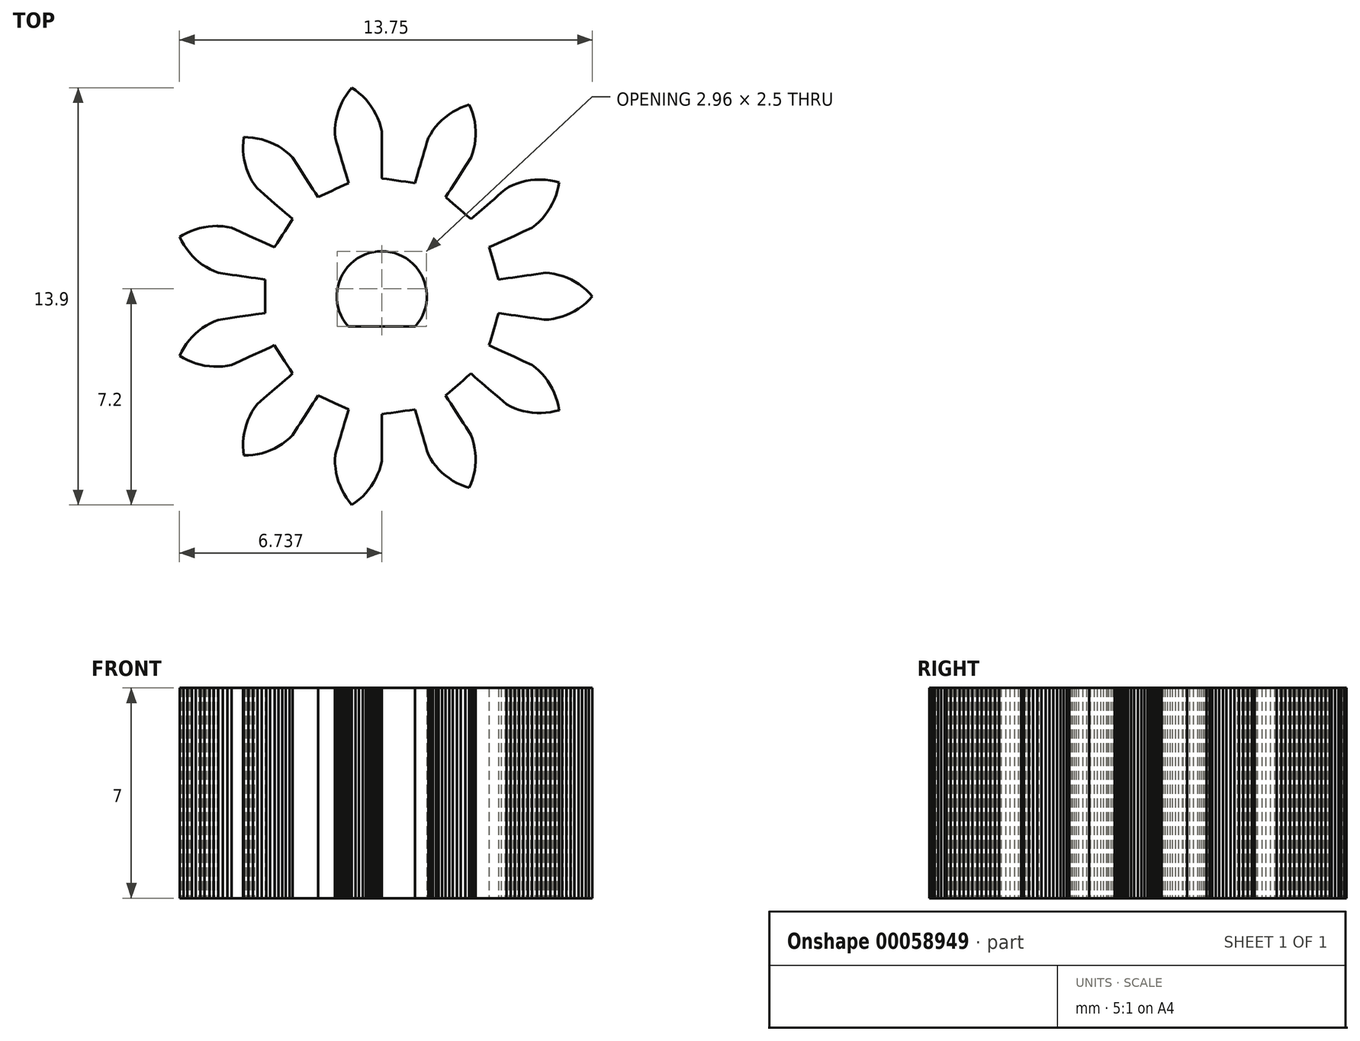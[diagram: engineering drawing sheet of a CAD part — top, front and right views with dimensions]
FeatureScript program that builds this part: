
annotation { "Feature Type Name" : "Feature", "Feature Type Description" : "" }
export const myFeature = defineFeature(function(context is Context, id is Id, definition is map)
    precondition{}
    {
        {
            var Q0;
            Q0=qCreatedBy(makeId("Top.planeOp"),FACE);
            var sketch = newSketch(context, id + "F0", { "sketchPlane" : qUnion([Q0])});
            skLineSegment(sketch, "E0", {"start": v(2.79, -0.56) * mm, "end": v(2.89, -0.57) * mm});
            skLineSegment(sketch, "E1", {"start": v(2.89, -0.57) * mm, "end": v(3.05, -0.6) * mm});
            skLineSegment(sketch, "E2", {"start": v(3.05, -0.6) * mm, "end": v(3.2, -0.62) * mm});
            skLineSegment(sketch, "E3", {"start": v(3.2, -0.62) * mm, "end": v(3.36, -0.64) * mm});
            skLineSegment(sketch, "E4", {"start": v(3.36, -0.64) * mm, "end": v(3.51, -0.66) * mm});
            skLineSegment(sketch, "E5", {"start": v(3.51, -0.66) * mm, "end": v(3.67, -0.69) * mm});
            skLineSegment(sketch, "E6", {"start": v(3.67, -0.69) * mm, "end": v(3.82, -0.7) * mm});
            skLineSegment(sketch, "E7", {"start": v(3.82, -0.7) * mm, "end": v(3.98, -0.73) * mm});
            skLineSegment(sketch, "E8", {"start": v(3.98, -0.73) * mm, "end": v(4.13, -0.75) * mm});
            skLineSegment(sketch, "E9", {"start": v(4.13, -0.75) * mm, "end": v(4.29, -0.78) * mm});
            skLineSegment(sketch, "E10", {"start": v(4.29, -0.78) * mm, "end": v(4.46, -0.77) * mm});
            skLineSegment(sketch, "E11", {"start": v(4.46, -0.77) * mm, "end": v(4.62, -0.75) * mm});
            skLineSegment(sketch, "E12", {"start": v(4.62, -0.75) * mm, "end": v(4.76, -0.72) * mm});
            skLineSegment(sketch, "E13", {"start": v(4.76, -0.72) * mm, "end": v(4.9, -0.67) * mm});
            skLineSegment(sketch, "E14", {"start": v(4.9, -0.67) * mm, "end": v(5.04, -0.63) * mm});
            skLineSegment(sketch, "E15", {"start": v(5.04, -0.63) * mm, "end": v(5.19, -0.56) * mm});
            skLineSegment(sketch, "E16", {"start": v(5.19, -0.56) * mm, "end": v(5.31, -0.5) * mm});
            skLineSegment(sketch, "E17", {"start": v(5.31, -0.5) * mm, "end": v(5.45, -0.41) * mm});
            skLineSegment(sketch, "E18", {"start": v(5.45, -0.41) * mm, "end": v(5.56, -0.33) * mm});
            skLineSegment(sketch, "E19", {"start": v(5.56, -0.33) * mm, "end": v(5.69, -0.23) * mm});
            skLineSegment(sketch, "E20", {"start": v(5.69, -0.23) * mm, "end": v(5.8, -0.13) * mm});
            skLineSegment(sketch, "E21", {"start": v(5.8, -0.13) * mm, "end": v(5.9, -0.02) * mm});
            skLineSegment(sketch, "E22", {"start": v(5.9, -0.02) * mm, "end": v(5.91, 0) * mm});
            skLineSegment(sketch, "E23", {"start": v(5.91, 0) * mm, "end": v(5.8, 0.12) * mm});
            skLineSegment(sketch, "E24", {"start": v(5.8, 0.12) * mm, "end": v(5.7, 0.22) * mm});
            skLineSegment(sketch, "E25", {"start": v(5.7, 0.22) * mm, "end": v(5.58, 0.32) * mm});
            skLineSegment(sketch, "E26", {"start": v(5.58, 0.32) * mm, "end": v(5.47, 0.4) * mm});
            skLineSegment(sketch, "E27", {"start": v(5.47, 0.4) * mm, "end": v(5.33, 0.48) * mm});
            skLineSegment(sketch, "E28", {"start": v(5.33, 0.48) * mm, "end": v(5.2, 0.55) * mm});
            skLineSegment(sketch, "E29", {"start": v(5.2, 0.55) * mm, "end": v(5.06, 0.62) * mm});
            skLineSegment(sketch, "E30", {"start": v(5.06, 0.62) * mm, "end": v(4.93, 0.67) * mm});
            skLineSegment(sketch, "E31", {"start": v(4.93, 0.67) * mm, "end": v(4.78, 0.71) * mm});
            skLineSegment(sketch, "E32", {"start": v(4.78, 0.71) * mm, "end": v(4.64, 0.75) * mm});
            skLineSegment(sketch, "E33", {"start": v(4.64, 0.75) * mm, "end": v(4.48, 0.77) * mm});
            skLineSegment(sketch, "E34", {"start": v(4.48, 0.77) * mm, "end": v(4.34, 0.78) * mm});
            skLineSegment(sketch, "E35", {"start": v(4.34, 0.78) * mm, "end": v(4.19, 0.76) * mm});
            skLineSegment(sketch, "E36", {"start": v(4.19, 0.76) * mm, "end": v(4.03, 0.74) * mm});
            skLineSegment(sketch, "E37", {"start": v(4.03, 0.74) * mm, "end": v(3.87, 0.72) * mm});
            skLineSegment(sketch, "E38", {"start": v(3.87, 0.72) * mm, "end": v(3.72, 0.7) * mm});
            skLineSegment(sketch, "E39", {"start": v(3.72, 0.7) * mm, "end": v(3.56, 0.67) * mm});
            skLineSegment(sketch, "E40", {"start": v(3.56, 0.67) * mm, "end": v(3.4, 0.65) * mm});
            skLineSegment(sketch, "E41", {"start": v(3.4, 0.65) * mm, "end": v(3.25, 0.63) * mm});
            skLineSegment(sketch, "E42", {"start": v(3.25, 0.63) * mm, "end": v(3.1, 0.6) * mm});
            skLineSegment(sketch, "E43", {"start": v(3.1, 0.6) * mm, "end": v(2.94, 0.58) * mm});
            skLineSegment(sketch, "E44", {"start": v(2.94, 0.58) * mm, "end": v(2.79, 0.56) * mm});
            skLineSegment(sketch, "E45", {"start": v(2.79, 0.56) * mm, "end": v(2.74, 0.71) * mm});
            skLineSegment(sketch, "E46", {"start": v(2.74, 0.71) * mm, "end": v(2.7, 0.86) * mm});
            skLineSegment(sketch, "E47", {"start": v(2.7, 0.86) * mm, "end": v(2.65, 1.01) * mm});
            skLineSegment(sketch, "E48", {"start": v(2.65, 1.01) * mm, "end": v(2.6, 1.16) * mm});
            skLineSegment(sketch, "E49", {"start": v(2.6, 1.16) * mm, "end": v(2.56, 1.31) * mm});
            skLineSegment(sketch, "E50", {"start": v(2.56, 1.31) * mm, "end": v(2.52, 1.47) * mm});
            skLineSegment(sketch, "E51", {"start": v(2.52, 1.47) * mm, "end": v(2.48, 1.62) * mm});
            skLineSegment(sketch, "E52", {"start": v(2.48, 1.62) * mm, "end": v(2.47, 1.63) * mm});
            skLineSegment(sketch, "E53", {"start": v(2.47, 1.63) * mm, "end": v(2.61, 1.7) * mm});
            skLineSegment(sketch, "E54", {"start": v(2.61, 1.7) * mm, "end": v(2.76, 1.76) * mm});
            skLineSegment(sketch, "E55", {"start": v(2.76, 1.76) * mm, "end": v(2.9, 1.83) * mm});
            skLineSegment(sketch, "E56", {"start": v(2.9, 1.83) * mm, "end": v(3.04, 1.9) * mm});
            skLineSegment(sketch, "E57", {"start": v(3.04, 1.9) * mm, "end": v(3.19, 1.96) * mm});
            skLineSegment(sketch, "E58", {"start": v(3.19, 1.96) * mm, "end": v(3.33, 2.02) * mm});
            skLineSegment(sketch, "E59", {"start": v(3.33, 2.02) * mm, "end": v(3.47, 2.09) * mm});
            skLineSegment(sketch, "E60", {"start": v(3.47, 2.09) * mm, "end": v(3.61, 2.15) * mm});
            skLineSegment(sketch, "E61", {"start": v(3.61, 2.15) * mm, "end": v(3.76, 2.22) * mm});
            skLineSegment(sketch, "E62", {"start": v(3.76, 2.22) * mm, "end": v(3.9, 2.28) * mm});
            skLineSegment(sketch, "E63", {"start": v(3.9, 2.28) * mm, "end": v(4.02, 2.38) * mm});
            skLineSegment(sketch, "E64", {"start": v(4.02, 2.38) * mm, "end": v(4.13, 2.48) * mm});
            skLineSegment(sketch, "E65", {"start": v(4.13, 2.48) * mm, "end": v(4.24, 2.6) * mm});
            skLineSegment(sketch, "E66", {"start": v(4.24, 2.6) * mm, "end": v(4.33, 2.7) * mm});
            skLineSegment(sketch, "E67", {"start": v(4.33, 2.7) * mm, "end": v(4.43, 2.83) * mm});
            skLineSegment(sketch, "E68", {"start": v(4.43, 2.83) * mm, "end": v(4.5, 2.95) * mm});
            skLineSegment(sketch, "E69", {"start": v(4.5, 2.95) * mm, "end": v(4.58, 3.09) * mm});
            skLineSegment(sketch, "E70", {"start": v(4.58, 3.09) * mm, "end": v(4.64, 3.22) * mm});
            skLineSegment(sketch, "E71", {"start": v(4.64, 3.22) * mm, "end": v(4.7, 3.36) * mm});
            skLineSegment(sketch, "E72", {"start": v(4.7, 3.36) * mm, "end": v(4.74, 3.5) * mm});
            skLineSegment(sketch, "E73", {"start": v(4.74, 3.5) * mm, "end": v(4.78, 3.65) * mm});
            skLineSegment(sketch, "E74", {"start": v(4.78, 3.65) * mm, "end": v(4.8, 3.8) * mm});
            skLineSegment(sketch, "E75", {"start": v(4.8, 3.8) * mm, "end": v(4.65, 3.83) * mm});
            skLineSegment(sketch, "E76", {"start": v(4.65, 3.83) * mm, "end": v(4.5, 3.86) * mm});
            skLineSegment(sketch, "E77", {"start": v(4.5, 3.86) * mm, "end": v(4.35, 3.88) * mm});
            skLineSegment(sketch, "E78", {"start": v(4.35, 3.88) * mm, "end": v(4.2, 3.89) * mm});
            skLineSegment(sketch, "E79", {"start": v(4.2, 3.89) * mm, "end": v(4.15, 3.89) * mm});
            skLineSegment(sketch, "E80", {"start": v(4.15, 3.89) * mm, "end": v(4, 3.88) * mm});
            skLineSegment(sketch, "E81", {"start": v(4, 3.88) * mm, "end": v(3.85, 3.87) * mm});
            skLineSegment(sketch, "E82", {"start": v(3.85, 3.87) * mm, "end": v(3.7, 3.84) * mm});
            skLineSegment(sketch, "E83", {"start": v(3.7, 3.84) * mm, "end": v(3.55, 3.8) * mm});
            skLineSegment(sketch, "E84", {"start": v(3.55, 3.8) * mm, "end": v(3.4, 3.76) * mm});
            skLineSegment(sketch, "E85", {"start": v(3.4, 3.76) * mm, "end": v(3.27, 3.7) * mm});
            skLineSegment(sketch, "E86", {"start": v(3.27, 3.7) * mm, "end": v(3.13, 3.64) * mm});
            skLineSegment(sketch, "E87", {"start": v(3.13, 3.64) * mm, "end": v(3, 3.55) * mm});
            skLineSegment(sketch, "E88", {"start": v(3, 3.55) * mm, "end": v(2.88, 3.45) * mm});
            skLineSegment(sketch, "E89", {"start": v(2.88, 3.45) * mm, "end": v(2.76, 3.35) * mm});
            skLineSegment(sketch, "E90", {"start": v(2.76, 3.35) * mm, "end": v(2.64, 3.24) * mm});
            skLineSegment(sketch, "E91", {"start": v(2.64, 3.24) * mm, "end": v(2.52, 3.14) * mm});
            skLineSegment(sketch, "E92", {"start": v(2.52, 3.14) * mm, "end": v(2.4, 3.04) * mm});
            skLineSegment(sketch, "E93", {"start": v(2.4, 3.04) * mm, "end": v(2.28, 2.93) * mm});
            skLineSegment(sketch, "E94", {"start": v(2.28, 2.93) * mm, "end": v(2.16, 2.83) * mm});
            skLineSegment(sketch, "E95", {"start": v(2.16, 2.83) * mm, "end": v(2.04, 2.73) * mm});
            skLineSegment(sketch, "E96", {"start": v(2.04, 2.73) * mm, "end": v(1.93, 2.62) * mm});
            skLineSegment(sketch, "E97", {"start": v(1.93, 2.62) * mm, "end": v(1.87, 2.57) * mm});
            skLineSegment(sketch, "E98", {"start": v(1.87, 2.57) * mm, "end": v(1.75, 2.68) * mm});
            skLineSegment(sketch, "E99", {"start": v(1.75, 2.68) * mm, "end": v(1.63, 2.78) * mm});
            skLineSegment(sketch, "E100", {"start": v(1.63, 2.78) * mm, "end": v(1.5, 2.88) * mm});
            skLineSegment(sketch, "E101", {"start": v(1.5, 2.88) * mm, "end": v(1.4, 2.99) * mm});
            skLineSegment(sketch, "E102", {"start": v(1.4, 2.99) * mm, "end": v(1.27, 3.09) * mm});
            skLineSegment(sketch, "E103", {"start": v(1.27, 3.09) * mm, "end": v(1.15, 3.2) * mm});
            skLineSegment(sketch, "E104", {"start": v(1.15, 3.2) * mm, "end": v(1.03, 3.3) * mm});
            skLineSegment(sketch, "E105", {"start": v(1.03, 3.3) * mm, "end": v(1.02, 3.3) * mm});
            skLineSegment(sketch, "E106", {"start": v(1.02, 3.3) * mm, "end": v(1.1, 3.44) * mm});
            skLineSegment(sketch, "E107", {"start": v(1.1, 3.44) * mm, "end": v(1.2, 3.57) * mm});
            skLineSegment(sketch, "E108", {"start": v(1.2, 3.57) * mm, "end": v(1.28, 3.7) * mm});
            skLineSegment(sketch, "E109", {"start": v(1.28, 3.7) * mm, "end": v(1.36, 3.83) * mm});
            skLineSegment(sketch, "E110", {"start": v(1.36, 3.83) * mm, "end": v(1.45, 3.97) * mm});
            skLineSegment(sketch, "E111", {"start": v(1.45, 3.97) * mm, "end": v(1.53, 4.1) * mm});
            skLineSegment(sketch, "E112", {"start": v(1.53, 4.1) * mm, "end": v(1.62, 4.23) * mm});
            skLineSegment(sketch, "E113", {"start": v(1.62, 4.23) * mm, "end": v(1.7, 4.36) * mm});
            skLineSegment(sketch, "E114", {"start": v(1.7, 4.36) * mm, "end": v(1.79, 4.5) * mm});
            skLineSegment(sketch, "E115", {"start": v(1.79, 4.5) * mm, "end": v(1.87, 4.63) * mm});
            skLineSegment(sketch, "E116", {"start": v(1.87, 4.63) * mm, "end": v(1.92, 4.78) * mm});
            skLineSegment(sketch, "E117", {"start": v(1.92, 4.78) * mm, "end": v(1.96, 4.91) * mm});
            skLineSegment(sketch, "E118", {"start": v(1.96, 4.91) * mm, "end": v(2, 5.07) * mm});
            skLineSegment(sketch, "E119", {"start": v(2, 5.07) * mm, "end": v(2.01, 5.21) * mm});
            skLineSegment(sketch, "E120", {"start": v(2.01, 5.21) * mm, "end": v(2.02, 5.37) * mm});
            skLineSegment(sketch, "E121", {"start": v(2.02, 5.37) * mm, "end": v(2.02, 5.51) * mm});
            skLineSegment(sketch, "E122", {"start": v(2.02, 5.51) * mm, "end": v(2, 5.67) * mm});
            skLineSegment(sketch, "E123", {"start": v(2, 5.67) * mm, "end": v(2, 5.81) * mm});
            skLineSegment(sketch, "E124", {"start": v(2, 5.81) * mm, "end": v(1.96, 5.96) * mm});
            skLineSegment(sketch, "E125", {"start": v(1.96, 5.96) * mm, "end": v(1.92, 6.1) * mm});
            skLineSegment(sketch, "E126", {"start": v(1.92, 6.1) * mm, "end": v(1.87, 6.25) * mm});
            skLineSegment(sketch, "E127", {"start": v(1.87, 6.25) * mm, "end": v(1.81, 6.38) * mm});
            skLineSegment(sketch, "E128", {"start": v(1.81, 6.38) * mm, "end": v(1.66, 6.33) * mm});
            skLineSegment(sketch, "E129", {"start": v(1.66, 6.33) * mm, "end": v(1.53, 6.28) * mm});
            skLineSegment(sketch, "E130", {"start": v(1.53, 6.28) * mm, "end": v(1.39, 6.21) * mm});
            skLineSegment(sketch, "E131", {"start": v(1.39, 6.21) * mm, "end": v(1.26, 6.14) * mm});
            skLineSegment(sketch, "E132", {"start": v(1.26, 6.14) * mm, "end": v(1.13, 6.06) * mm});
            skLineSegment(sketch, "E133", {"start": v(1.13, 6.06) * mm, "end": v(1.02, 5.97) * mm});
            skLineSegment(sketch, "E134", {"start": v(1.02, 5.97) * mm, "end": v(0.9, 5.87) * mm});
            skLineSegment(sketch, "E135", {"start": v(0.9, 5.87) * mm, "end": v(0.8, 5.77) * mm});
            skLineSegment(sketch, "E136", {"start": v(0.8, 5.77) * mm, "end": v(0.7, 5.65) * mm});
            skLineSegment(sketch, "E137", {"start": v(0.7, 5.65) * mm, "end": v(0.6, 5.53) * mm});
            skLineSegment(sketch, "E138", {"start": v(0.6, 5.53) * mm, "end": v(0.52, 5.4) * mm});
            skLineSegment(sketch, "E139", {"start": v(0.52, 5.4) * mm, "end": v(0.45, 5.28) * mm});
            skLineSegment(sketch, "E140", {"start": v(0.45, 5.28) * mm, "end": v(0.4, 5.13) * mm});
            skLineSegment(sketch, "E141", {"start": v(0.4, 5.13) * mm, "end": v(0.36, 4.98) * mm});
            skLineSegment(sketch, "E142", {"start": v(0.36, 4.98) * mm, "end": v(0.31, 4.83) * mm});
            skLineSegment(sketch, "E143", {"start": v(0.31, 4.83) * mm, "end": v(0.27, 4.67) * mm});
            skLineSegment(sketch, "E144", {"start": v(0.27, 4.67) * mm, "end": v(0.22, 4.52) * mm});
            skLineSegment(sketch, "E145", {"start": v(0.22, 4.52) * mm, "end": v(0.18, 4.37) * mm});
            skLineSegment(sketch, "E146", {"start": v(0.18, 4.37) * mm, "end": v(0.14, 4.22) * mm});
            skLineSegment(sketch, "E147", {"start": v(0.14, 4.22) * mm, "end": v(0.1, 4.07) * mm});
            skLineSegment(sketch, "E148", {"start": v(0.1, 4.07) * mm, "end": v(0.05, 3.92) * mm});
            skLineSegment(sketch, "E149", {"start": v(0.05, 3.92) * mm, "end": v(0, 3.77) * mm});
            skLineSegment(sketch, "E150", {"start": v(0, 3.77) * mm, "end": v(-0.15, 3.8) * mm});
            skLineSegment(sketch, "E151", {"start": v(-0.15, 3.8) * mm, "end": v(-0.3, 3.81) * mm});
            skLineSegment(sketch, "E152", {"start": v(-0.3, 3.81) * mm, "end": v(-0.46, 3.84) * mm});
            skLineSegment(sketch, "E153", {"start": v(-0.46, 3.84) * mm, "end": v(-0.62, 3.86) * mm});
            skLineSegment(sketch, "E154", {"start": v(-0.62, 3.86) * mm, "end": v(-0.78, 3.88) * mm});
            skLineSegment(sketch, "E155", {"start": v(-0.78, 3.88) * mm, "end": v(-0.93, 3.9) * mm});
            skLineSegment(sketch, "E156", {"start": v(-0.93, 3.9) * mm, "end": v(-1.09, 3.93) * mm});
            skLineSegment(sketch, "E157", {"start": v(-1.09, 3.93) * mm, "end": v(-1.1, 3.93) * mm});
            skLineSegment(sketch, "E158", {"start": v(-1.1, 3.93) * mm, "end": v(-1.1, 4.09) * mm});
            skLineSegment(sketch, "E159", {"start": v(-1.1, 4.09) * mm, "end": v(-1.1, 4.24) * mm});
            skLineSegment(sketch, "E160", {"start": v(-1.1, 4.24) * mm, "end": v(-1.1, 4.4) * mm});
            skLineSegment(sketch, "E161", {"start": v(-1.1, 4.4) * mm, "end": v(-1.1, 4.56) * mm});
            skLineSegment(sketch, "E162", {"start": v(-1.1, 4.56) * mm, "end": v(-1.1, 4.71) * mm});
            skLineSegment(sketch, "E163", {"start": v(-1.1, 4.71) * mm, "end": v(-1.1, 4.87) * mm});
            skLineSegment(sketch, "E164", {"start": v(-1.1, 4.87) * mm, "end": v(-1.1, 5.03) * mm});
            skLineSegment(sketch, "E165", {"start": v(-1.1, 5.03) * mm, "end": v(-1.1, 5.19) * mm});
            skLineSegment(sketch, "E166", {"start": v(-1.1, 5.19) * mm, "end": v(-1.1, 5.34) * mm});
            skLineSegment(sketch, "E167", {"start": v(-1.1, 5.34) * mm, "end": v(-1.1, 5.5) * mm});
            skLineSegment(sketch, "E168", {"start": v(-1.1, 5.5) * mm, "end": v(-1.14, 5.65) * mm});
            skLineSegment(sketch, "E169", {"start": v(-1.14, 5.65) * mm, "end": v(-1.18, 5.8) * mm});
            skLineSegment(sketch, "E170", {"start": v(-1.18, 5.8) * mm, "end": v(-1.24, 5.94) * mm});
            skLineSegment(sketch, "E171", {"start": v(-1.24, 5.94) * mm, "end": v(-1.3, 6.07) * mm});
            skLineSegment(sketch, "E172", {"start": v(-1.3, 6.07) * mm, "end": v(-1.38, 6.2) * mm});
            skLineSegment(sketch, "E173", {"start": v(-1.38, 6.2) * mm, "end": v(-1.45, 6.33) * mm});
            skLineSegment(sketch, "E174", {"start": v(-1.45, 6.33) * mm, "end": v(-1.55, 6.45) * mm});
            skLineSegment(sketch, "E175", {"start": v(-1.55, 6.45) * mm, "end": v(-1.64, 6.56) * mm});
            skLineSegment(sketch, "E176", {"start": v(-1.64, 6.56) * mm, "end": v(-1.75, 6.67) * mm});
            skLineSegment(sketch, "E177", {"start": v(-1.75, 6.67) * mm, "end": v(-1.86, 6.77) * mm});
            skLineSegment(sketch, "E178", {"start": v(-1.86, 6.77) * mm, "end": v(-1.98, 6.86) * mm});
            skLineSegment(sketch, "E179", {"start": v(-1.98, 6.86) * mm, "end": v(-2.1, 6.95) * mm});
            skLineSegment(sketch, "E180", {"start": v(-2.1, 6.95) * mm, "end": v(-2.2, 6.82) * mm});
            skLineSegment(sketch, "E181", {"start": v(-2.2, 6.82) * mm, "end": v(-2.29, 6.7) * mm});
            skLineSegment(sketch, "E182", {"start": v(-2.29, 6.7) * mm, "end": v(-2.37, 6.57) * mm});
            skLineSegment(sketch, "E183", {"start": v(-2.37, 6.57) * mm, "end": v(-2.43, 6.45) * mm});
            skLineSegment(sketch, "E184", {"start": v(-2.43, 6.45) * mm, "end": v(-2.5, 6.3) * mm});
            skLineSegment(sketch, "E185", {"start": v(-2.5, 6.3) * mm, "end": v(-2.55, 6.17) * mm});
            skLineSegment(sketch, "E186", {"start": v(-2.55, 6.17) * mm, "end": v(-2.6, 6.02) * mm});
            skLineSegment(sketch, "E187", {"start": v(-2.6, 6.02) * mm, "end": v(-2.62, 5.88) * mm});
            skLineSegment(sketch, "E188", {"start": v(-2.62, 5.88) * mm, "end": v(-2.65, 5.72) * mm});
            skLineSegment(sketch, "E189", {"start": v(-2.65, 5.72) * mm, "end": v(-2.66, 5.58) * mm});
            skLineSegment(sketch, "E190", {"start": v(-2.66, 5.58) * mm, "end": v(-2.66, 5.42) * mm});
            skLineSegment(sketch, "E191", {"start": v(-2.66, 5.42) * mm, "end": v(-2.65, 5.28) * mm});
            skLineSegment(sketch, "E192", {"start": v(-2.65, 5.28) * mm, "end": v(-2.6, 5.13) * mm});
            skLineSegment(sketch, "E193", {"start": v(-2.6, 5.13) * mm, "end": v(-2.56, 4.98) * mm});
            skLineSegment(sketch, "E194", {"start": v(-2.56, 4.98) * mm, "end": v(-2.52, 4.83) * mm});
            skLineSegment(sketch, "E195", {"start": v(-2.52, 4.83) * mm, "end": v(-2.48, 4.67) * mm});
            skLineSegment(sketch, "E196", {"start": v(-2.48, 4.67) * mm, "end": v(-2.43, 4.52) * mm});
            skLineSegment(sketch, "E197", {"start": v(-2.43, 4.52) * mm, "end": v(-2.39, 4.37) * mm});
            skLineSegment(sketch, "E198", {"start": v(-2.39, 4.37) * mm, "end": v(-2.34, 4.22) * mm});
            skLineSegment(sketch, "E199", {"start": v(-2.34, 4.22) * mm, "end": v(-2.3, 4.07) * mm});
            skLineSegment(sketch, "E200", {"start": v(-2.3, 4.07) * mm, "end": v(-2.25, 3.92) * mm});
            skLineSegment(sketch, "E201", {"start": v(-2.25, 3.92) * mm, "end": v(-2.21, 3.77) * mm});
            skLineSegment(sketch, "E202", {"start": v(-2.21, 3.77) * mm, "end": v(-2.35, 3.7) * mm});
            skLineSegment(sketch, "E203", {"start": v(-2.35, 3.7) * mm, "end": v(-2.5, 3.64) * mm});
            skLineSegment(sketch, "E204", {"start": v(-2.5, 3.64) * mm, "end": v(-2.64, 3.57) * mm});
            skLineSegment(sketch, "E205", {"start": v(-2.64, 3.57) * mm, "end": v(-2.78, 3.5) * mm});
            skLineSegment(sketch, "E206", {"start": v(-2.78, 3.5) * mm, "end": v(-2.93, 3.44) * mm});
            skLineSegment(sketch, "E207", {"start": v(-2.93, 3.44) * mm, "end": v(-3.07, 3.38) * mm});
            skLineSegment(sketch, "E208", {"start": v(-3.07, 3.38) * mm, "end": v(-3.21, 3.31) * mm});
            skLineSegment(sketch, "E209", {"start": v(-3.21, 3.31) * mm, "end": v(-3.23, 3.3) * mm});
            skLineSegment(sketch, "E210", {"start": v(-3.23, 3.3) * mm, "end": v(-3.31, 3.44) * mm});
            skLineSegment(sketch, "E211", {"start": v(-3.31, 3.44) * mm, "end": v(-3.4, 3.57) * mm});
            skLineSegment(sketch, "E212", {"start": v(-3.4, 3.57) * mm, "end": v(-3.48, 3.7) * mm});
            skLineSegment(sketch, "E213", {"start": v(-3.48, 3.7) * mm, "end": v(-3.57, 3.83) * mm});
            skLineSegment(sketch, "E214", {"start": v(-3.57, 3.83) * mm, "end": v(-3.65, 3.97) * mm});
            skLineSegment(sketch, "E215", {"start": v(-3.65, 3.97) * mm, "end": v(-3.74, 4.1) * mm});
            skLineSegment(sketch, "E216", {"start": v(-3.74, 4.1) * mm, "end": v(-3.82, 4.23) * mm});
            skLineSegment(sketch, "E217", {"start": v(-3.82, 4.23) * mm, "end": v(-3.9, 4.36) * mm});
            skLineSegment(sketch, "E218", {"start": v(-3.9, 4.36) * mm, "end": v(-4, 4.5) * mm});
            skLineSegment(sketch, "E219", {"start": v(-4, 4.5) * mm, "end": v(-4.08, 4.63) * mm});
            skLineSegment(sketch, "E220", {"start": v(-4.08, 4.63) * mm, "end": v(-4.2, 4.74) * mm});
            skLineSegment(sketch, "E221", {"start": v(-4.2, 4.74) * mm, "end": v(-4.3, 4.83) * mm});
            skLineSegment(sketch, "E222", {"start": v(-4.3, 4.83) * mm, "end": v(-4.43, 4.92) * mm});
            skLineSegment(sketch, "E223", {"start": v(-4.43, 4.92) * mm, "end": v(-4.55, 5) * mm});
            skLineSegment(sketch, "E224", {"start": v(-4.55, 5) * mm, "end": v(-4.69, 5.07) * mm});
            skLineSegment(sketch, "E225", {"start": v(-4.69, 5.07) * mm, "end": v(-4.82, 5.13) * mm});
            skLineSegment(sketch, "E226", {"start": v(-4.82, 5.13) * mm, "end": v(-4.97, 5.19) * mm});
            skLineSegment(sketch, "E227", {"start": v(-4.97, 5.19) * mm, "end": v(-5.1, 5.23) * mm});
            skLineSegment(sketch, "E228", {"start": v(-5.1, 5.23) * mm, "end": v(-5.26, 5.26) * mm});
            skLineSegment(sketch, "E229", {"start": v(-5.26, 5.26) * mm, "end": v(-5.4, 5.29) * mm});
            skLineSegment(sketch, "E230", {"start": v(-5.4, 5.29) * mm, "end": v(-5.56, 5.3) * mm});
            skLineSegment(sketch, "E231", {"start": v(-5.56, 5.3) * mm, "end": v(-5.7, 5.3) * mm});
            skLineSegment(sketch, "E232", {"start": v(-5.7, 5.3) * mm, "end": v(-5.72, 5.15) * mm});
            skLineSegment(sketch, "E233", {"start": v(-5.72, 5.15) * mm, "end": v(-5.72, 5) * mm});
            skLineSegment(sketch, "E234", {"start": v(-5.72, 5) * mm, "end": v(-5.72, 4.85) * mm});
            skLineSegment(sketch, "E235", {"start": v(-5.72, 4.85) * mm, "end": v(-5.7, 4.7) * mm});
            skLineSegment(sketch, "E236", {"start": v(-5.7, 4.7) * mm, "end": v(-5.68, 4.55) * mm});
            skLineSegment(sketch, "E237", {"start": v(-5.68, 4.55) * mm, "end": v(-5.65, 4.4) * mm});
            skLineSegment(sketch, "E238", {"start": v(-5.65, 4.4) * mm, "end": v(-5.6, 4.26) * mm});
            skLineSegment(sketch, "E239", {"start": v(-5.6, 4.26) * mm, "end": v(-5.56, 4.12) * mm});
            skLineSegment(sketch, "E240", {"start": v(-5.56, 4.12) * mm, "end": v(-5.5, 3.98) * mm});
            skLineSegment(sketch, "E241", {"start": v(-5.5, 3.98) * mm, "end": v(-5.43, 3.85) * mm});
            skLineSegment(sketch, "E242", {"start": v(-5.43, 3.85) * mm, "end": v(-5.34, 3.72) * mm});
            skLineSegment(sketch, "E243", {"start": v(-5.34, 3.72) * mm, "end": v(-5.26, 3.6) * mm});
            skLineSegment(sketch, "E244", {"start": v(-5.26, 3.6) * mm, "end": v(-5.14, 3.5) * mm});
            skLineSegment(sketch, "E245", {"start": v(-5.14, 3.5) * mm, "end": v(-5.02, 3.4) * mm});
            skLineSegment(sketch, "E246", {"start": v(-5.02, 3.4) * mm, "end": v(-4.9, 3.3) * mm});
            skLineSegment(sketch, "E247", {"start": v(-4.9, 3.3) * mm, "end": v(-4.79, 3.2) * mm});
            skLineSegment(sketch, "E248", {"start": v(-4.79, 3.2) * mm, "end": v(-4.67, 3.09) * mm});
            skLineSegment(sketch, "E249", {"start": v(-4.67, 3.09) * mm, "end": v(-4.55, 2.98) * mm});
            skLineSegment(sketch, "E250", {"start": v(-4.55, 2.98) * mm, "end": v(-4.43, 2.88) * mm});
            skLineSegment(sketch, "E251", {"start": v(-4.43, 2.88) * mm, "end": v(-4.31, 2.78) * mm});
            skLineSegment(sketch, "E252", {"start": v(-4.31, 2.78) * mm, "end": v(-4.2, 2.68) * mm});
            skLineSegment(sketch, "E253", {"start": v(-4.2, 2.68) * mm, "end": v(-4.07, 2.57) * mm});
            skLineSegment(sketch, "E254", {"start": v(-4.07, 2.57) * mm, "end": v(-4.16, 2.44) * mm});
            skLineSegment(sketch, "E255", {"start": v(-4.16, 2.44) * mm, "end": v(-4.24, 2.3) * mm});
            skLineSegment(sketch, "E256", {"start": v(-4.24, 2.3) * mm, "end": v(-4.33, 2.18) * mm});
            skLineSegment(sketch, "E257", {"start": v(-4.33, 2.18) * mm, "end": v(-4.41, 2.04) * mm});
            skLineSegment(sketch, "E258", {"start": v(-4.41, 2.04) * mm, "end": v(-4.5, 1.91) * mm});
            skLineSegment(sketch, "E259", {"start": v(-4.5, 1.91) * mm, "end": v(-4.58, 1.78) * mm});
            skLineSegment(sketch, "E260", {"start": v(-4.58, 1.78) * mm, "end": v(-4.67, 1.65) * mm});
            skLineSegment(sketch, "E261", {"start": v(-4.67, 1.65) * mm, "end": v(-4.68, 1.63) * mm});
            skLineSegment(sketch, "E262", {"start": v(-4.68, 1.63) * mm, "end": v(-4.82, 1.7) * mm});
            skLineSegment(sketch, "E263", {"start": v(-4.82, 1.7) * mm, "end": v(-4.96, 1.76) * mm});
            skLineSegment(sketch, "E264", {"start": v(-4.96, 1.76) * mm, "end": v(-5.1, 1.83) * mm});
            skLineSegment(sketch, "E265", {"start": v(-5.1, 1.83) * mm, "end": v(-5.25, 1.9) * mm});
            skLineSegment(sketch, "E266", {"start": v(-5.25, 1.9) * mm, "end": v(-5.4, 1.96) * mm});
            skLineSegment(sketch, "E267", {"start": v(-5.4, 1.96) * mm, "end": v(-5.53, 2.02) * mm});
            skLineSegment(sketch, "E268", {"start": v(-5.53, 2.02) * mm, "end": v(-5.68, 2.09) * mm});
            skLineSegment(sketch, "E269", {"start": v(-5.68, 2.09) * mm, "end": v(-5.82, 2.15) * mm});
            skLineSegment(sketch, "E270", {"start": v(-5.82, 2.15) * mm, "end": v(-5.96, 2.22) * mm});
            skLineSegment(sketch, "E271", {"start": v(-5.96, 2.22) * mm, "end": v(-6.1, 2.28) * mm});
            skLineSegment(sketch, "E272", {"start": v(-6.1, 2.28) * mm, "end": v(-6.26, 2.31) * mm});
            skLineSegment(sketch, "E273", {"start": v(-6.26, 2.31) * mm, "end": v(-6.4, 2.33) * mm});
            skLineSegment(sketch, "E274", {"start": v(-6.4, 2.33) * mm, "end": v(-6.56, 2.34) * mm});
            skLineSegment(sketch, "E275", {"start": v(-6.56, 2.34) * mm, "end": v(-6.58, 2.34) * mm});
            skLineSegment(sketch, "E276", {"start": v(-6.58, 2.34) * mm, "end": v(-6.74, 2.34) * mm});
            skLineSegment(sketch, "E277", {"start": v(-6.74, 2.34) * mm, "end": v(-6.88, 2.33) * mm});
            skLineSegment(sketch, "E278", {"start": v(-6.88, 2.33) * mm, "end": v(-7.04, 2.3) * mm});
            skLineSegment(sketch, "E279", {"start": v(-7.04, 2.3) * mm, "end": v(-7.18, 2.27) * mm});
            skLineSegment(sketch, "E280", {"start": v(-7.18, 2.27) * mm, "end": v(-7.33, 2.22) * mm});
            skLineSegment(sketch, "E281", {"start": v(-7.33, 2.22) * mm, "end": v(-7.46, 2.17) * mm});
            skLineSegment(sketch, "E282", {"start": v(-7.46, 2.17) * mm, "end": v(-7.6, 2.1) * mm});
            skLineSegment(sketch, "E283", {"start": v(-7.6, 2.1) * mm, "end": v(-7.73, 2.04) * mm});
            skLineSegment(sketch, "E284", {"start": v(-7.73, 2.04) * mm, "end": v(-7.84, 1.98) * mm});
            skLineSegment(sketch, "E285", {"start": v(-7.84, 1.98) * mm, "end": v(-7.77, 1.84) * mm});
            skLineSegment(sketch, "E286", {"start": v(-7.77, 1.84) * mm, "end": v(-7.7, 1.71) * mm});
            skLineSegment(sketch, "E287", {"start": v(-7.7, 1.71) * mm, "end": v(-7.6, 1.58) * mm});
            skLineSegment(sketch, "E288", {"start": v(-7.6, 1.58) * mm, "end": v(-7.52, 1.47) * mm});
            skLineSegment(sketch, "E289", {"start": v(-7.52, 1.47) * mm, "end": v(-7.42, 1.35) * mm});
            skLineSegment(sketch, "E290", {"start": v(-7.42, 1.35) * mm, "end": v(-7.31, 1.25) * mm});
            skLineSegment(sketch, "E291", {"start": v(-7.31, 1.25) * mm, "end": v(-7.2, 1.15) * mm});
            skLineSegment(sketch, "E292", {"start": v(-7.2, 1.15) * mm, "end": v(-7.08, 1.06) * mm});
            skLineSegment(sketch, "E293", {"start": v(-7.08, 1.06) * mm, "end": v(-6.95, 0.97) * mm});
            skLineSegment(sketch, "E294", {"start": v(-6.95, 0.97) * mm, "end": v(-6.82, 0.9) * mm});
            skLineSegment(sketch, "E295", {"start": v(-6.82, 0.9) * mm, "end": v(-6.68, 0.84) * mm});
            skLineSegment(sketch, "E296", {"start": v(-6.68, 0.84) * mm, "end": v(-6.55, 0.78) * mm});
            skLineSegment(sketch, "E297", {"start": v(-6.55, 0.78) * mm, "end": v(-6.4, 0.76) * mm});
            skLineSegment(sketch, "E298", {"start": v(-6.4, 0.76) * mm, "end": v(-6.24, 0.74) * mm});
            skLineSegment(sketch, "E299", {"start": v(-6.24, 0.74) * mm, "end": v(-6.08, 0.72) * mm});
            skLineSegment(sketch, "E300", {"start": v(-6.08, 0.72) * mm, "end": v(-5.93, 0.7) * mm});
            skLineSegment(sketch, "E301", {"start": v(-5.93, 0.7) * mm, "end": v(-5.77, 0.67) * mm});
            skLineSegment(sketch, "E302", {"start": v(-5.77, 0.67) * mm, "end": v(-5.61, 0.65) * mm});
            skLineSegment(sketch, "E303", {"start": v(-5.61, 0.65) * mm, "end": v(-5.46, 0.63) * mm});
            skLineSegment(sketch, "E304", {"start": v(-5.46, 0.63) * mm, "end": v(-5.3, 0.6) * mm});
            skLineSegment(sketch, "E305", {"start": v(-5.3, 0.6) * mm, "end": v(-5.15, 0.58) * mm});
            skLineSegment(sketch, "E306", {"start": v(-5.15, 0.58) * mm, "end": v(-5, 0.56) * mm});
            skLineSegment(sketch, "E307", {"start": v(-5, 0.56) * mm, "end": v(-5, 0.4) * mm});
            skLineSegment(sketch, "E308", {"start": v(-5, 0.4) * mm, "end": v(-5, 0.24) * mm});
            skLineSegment(sketch, "E309", {"start": v(-5, 0.24) * mm, "end": v(-5, 0.09) * mm});
            skLineSegment(sketch, "E310", {"start": v(-5, 0.09) * mm, "end": v(-5, -0.07) * mm});
            skLineSegment(sketch, "E311", {"start": v(-5, -0.07) * mm, "end": v(-5, -0.23) * mm});
            skLineSegment(sketch, "E312", {"start": v(-5, -0.23) * mm, "end": v(-5, -0.39) * mm});
            skLineSegment(sketch, "E313", {"start": v(-5, -0.39) * mm, "end": v(-5, -0.54) * mm});
            skLineSegment(sketch, "E314", {"start": v(-5, -0.54) * mm, "end": v(-5, -0.56) * mm});
            skLineSegment(sketch, "E315", {"start": v(-5, -0.56) * mm, "end": v(-5.15, -0.58) * mm});
            skLineSegment(sketch, "E316", {"start": v(-5.15, -0.58) * mm, "end": v(-5.3, -0.6) * mm});
            skLineSegment(sketch, "E317", {"start": v(-5.3, -0.6) * mm, "end": v(-5.46, -0.63) * mm});
            skLineSegment(sketch, "E318", {"start": v(-5.46, -0.63) * mm, "end": v(-5.61, -0.65) * mm});
            skLineSegment(sketch, "E319", {"start": v(-5.61, -0.65) * mm, "end": v(-5.77, -0.67) * mm});
            skLineSegment(sketch, "E320", {"start": v(-5.77, -0.67) * mm, "end": v(-5.93, -0.7) * mm});
            skLineSegment(sketch, "E321", {"start": v(-5.93, -0.7) * mm, "end": v(-6.08, -0.72) * mm});
            skLineSegment(sketch, "E322", {"start": v(-6.08, -0.72) * mm, "end": v(-6.24, -0.74) * mm});
            skLineSegment(sketch, "E323", {"start": v(-6.24, -0.74) * mm, "end": v(-6.4, -0.76) * mm});
            skLineSegment(sketch, "E324", {"start": v(-6.4, -0.76) * mm, "end": v(-6.55, -0.78) * mm});
            skLineSegment(sketch, "E325", {"start": v(-6.55, -0.78) * mm, "end": v(-6.7, -0.84) * mm});
            skLineSegment(sketch, "E326", {"start": v(-6.7, -0.84) * mm, "end": v(-6.82, -0.9) * mm});
            skLineSegment(sketch, "E327", {"start": v(-6.82, -0.9) * mm, "end": v(-6.96, -0.98) * mm});
            skLineSegment(sketch, "E328", {"start": v(-6.96, -0.98) * mm, "end": v(-7.08, -1.06) * mm});
            skLineSegment(sketch, "E329", {"start": v(-7.08, -1.06) * mm, "end": v(-7.2, -1.15) * mm});
            skLineSegment(sketch, "E330", {"start": v(-7.2, -1.15) * mm, "end": v(-7.31, -1.25) * mm});
            skLineSegment(sketch, "E331", {"start": v(-7.31, -1.25) * mm, "end": v(-7.43, -1.36) * mm});
            skLineSegment(sketch, "E332", {"start": v(-7.43, -1.36) * mm, "end": v(-7.52, -1.47) * mm});
            skLineSegment(sketch, "E333", {"start": v(-7.52, -1.47) * mm, "end": v(-7.62, -1.6) * mm});
            skLineSegment(sketch, "E334", {"start": v(-7.62, -1.6) * mm, "end": v(-7.7, -1.71) * mm});
            skLineSegment(sketch, "E335", {"start": v(-7.7, -1.71) * mm, "end": v(-7.77, -1.85) * mm});
            skLineSegment(sketch, "E336", {"start": v(-7.77, -1.85) * mm, "end": v(-7.84, -1.98) * mm});
            skLineSegment(sketch, "E337", {"start": v(-7.84, -1.98) * mm, "end": v(-7.7, -2.06) * mm});
            skLineSegment(sketch, "E338", {"start": v(-7.7, -2.06) * mm, "end": v(-7.57, -2.12) * mm});
            skLineSegment(sketch, "E339", {"start": v(-7.57, -2.12) * mm, "end": v(-7.43, -2.19) * mm});
            skLineSegment(sketch, "E340", {"start": v(-7.43, -2.19) * mm, "end": v(-7.3, -2.24) * mm});
            skLineSegment(sketch, "E341", {"start": v(-7.3, -2.24) * mm, "end": v(-7.14, -2.28) * mm});
            skLineSegment(sketch, "E342", {"start": v(-7.14, -2.28) * mm, "end": v(-7, -2.3) * mm});
            skLineSegment(sketch, "E343", {"start": v(-7, -2.3) * mm, "end": v(-6.85, -2.33) * mm});
            skLineSegment(sketch, "E344", {"start": v(-6.85, -2.33) * mm, "end": v(-6.7, -2.34) * mm});
            skLineSegment(sketch, "E345", {"start": v(-6.7, -2.34) * mm, "end": v(-6.55, -2.34) * mm});
            skLineSegment(sketch, "E346", {"start": v(-6.55, -2.34) * mm, "end": v(-6.4, -2.33) * mm});
            skLineSegment(sketch, "E347", {"start": v(-6.4, -2.33) * mm, "end": v(-6.25, -2.31) * mm});
            skLineSegment(sketch, "E348", {"start": v(-6.25, -2.31) * mm, "end": v(-6.1, -2.28) * mm});
            skLineSegment(sketch, "E349", {"start": v(-6.1, -2.28) * mm, "end": v(-5.96, -2.22) * mm});
            skLineSegment(sketch, "E350", {"start": v(-5.96, -2.22) * mm, "end": v(-5.82, -2.15) * mm});
            skLineSegment(sketch, "E351", {"start": v(-5.82, -2.15) * mm, "end": v(-5.68, -2.09) * mm});
            skLineSegment(sketch, "E352", {"start": v(-5.68, -2.09) * mm, "end": v(-5.53, -2.02) * mm});
            skLineSegment(sketch, "E353", {"start": v(-5.53, -2.02) * mm, "end": v(-5.4, -1.96) * mm});
            skLineSegment(sketch, "E354", {"start": v(-5.4, -1.96) * mm, "end": v(-5.25, -1.9) * mm});
            skLineSegment(sketch, "E355", {"start": v(-5.25, -1.9) * mm, "end": v(-5.1, -1.83) * mm});
            skLineSegment(sketch, "E356", {"start": v(-5.1, -1.83) * mm, "end": v(-4.96, -1.76) * mm});
            skLineSegment(sketch, "E357", {"start": v(-4.96, -1.76) * mm, "end": v(-4.82, -1.7) * mm});
            skLineSegment(sketch, "E358", {"start": v(-4.82, -1.7) * mm, "end": v(-4.68, -1.63) * mm});
            skLineSegment(sketch, "E359", {"start": v(-4.68, -1.63) * mm, "end": v(-4.6, -1.76) * mm});
            skLineSegment(sketch, "E360", {"start": v(-4.6, -1.76) * mm, "end": v(-4.5, -1.9) * mm});
            skLineSegment(sketch, "E361", {"start": v(-4.5, -1.9) * mm, "end": v(-4.42, -2.03) * mm});
            skLineSegment(sketch, "E362", {"start": v(-4.42, -2.03) * mm, "end": v(-4.34, -2.16) * mm});
            skLineSegment(sketch, "E363", {"start": v(-4.34, -2.16) * mm, "end": v(-4.25, -2.3) * mm});
            skLineSegment(sketch, "E364", {"start": v(-4.25, -2.3) * mm, "end": v(-4.17, -2.43) * mm});
            skLineSegment(sketch, "E365", {"start": v(-4.17, -2.43) * mm, "end": v(-4.08, -2.56) * mm});
            skLineSegment(sketch, "E366", {"start": v(-4.08, -2.56) * mm, "end": v(-4.07, -2.57) * mm});
            skLineSegment(sketch, "E367", {"start": v(-4.07, -2.57) * mm, "end": v(-4.2, -2.68) * mm});
            skLineSegment(sketch, "E368", {"start": v(-4.2, -2.68) * mm, "end": v(-4.31, -2.78) * mm});
            skLineSegment(sketch, "E369", {"start": v(-4.31, -2.78) * mm, "end": v(-4.43, -2.88) * mm});
            skLineSegment(sketch, "E370", {"start": v(-4.43, -2.88) * mm, "end": v(-4.55, -2.98) * mm});
            skLineSegment(sketch, "E371", {"start": v(-4.55, -2.98) * mm, "end": v(-4.67, -3.09) * mm});
            skLineSegment(sketch, "E372", {"start": v(-4.67, -3.09) * mm, "end": v(-4.79, -3.2) * mm});
            skLineSegment(sketch, "E373", {"start": v(-4.79, -3.2) * mm, "end": v(-4.9, -3.3) * mm});
            skLineSegment(sketch, "E374", {"start": v(-4.9, -3.3) * mm, "end": v(-5.02, -3.4) * mm});
            skLineSegment(sketch, "E375", {"start": v(-5.02, -3.4) * mm, "end": v(-5.14, -3.5) * mm});
            skLineSegment(sketch, "E376", {"start": v(-5.14, -3.5) * mm, "end": v(-5.26, -3.6) * mm});
            skLineSegment(sketch, "E377", {"start": v(-5.26, -3.6) * mm, "end": v(-5.35, -3.73) * mm});
            skLineSegment(sketch, "E378", {"start": v(-5.35, -3.73) * mm, "end": v(-5.43, -3.85) * mm});
            skLineSegment(sketch, "E379", {"start": v(-5.43, -3.85) * mm, "end": v(-5.5, -4) * mm});
            skLineSegment(sketch, "E380", {"start": v(-5.5, -4) * mm, "end": v(-5.56, -4.12) * mm});
            skLineSegment(sketch, "E381", {"start": v(-5.56, -4.12) * mm, "end": v(-5.61, -4.27) * mm});
            skLineSegment(sketch, "E382", {"start": v(-5.61, -4.27) * mm, "end": v(-5.65, -4.4) * mm});
            skLineSegment(sketch, "E383", {"start": v(-5.65, -4.4) * mm, "end": v(-5.69, -4.56) * mm});
            skLineSegment(sketch, "E384", {"start": v(-5.69, -4.56) * mm, "end": v(-5.7, -4.7) * mm});
            skLineSegment(sketch, "E385", {"start": v(-5.7, -4.7) * mm, "end": v(-5.72, -4.86) * mm});
            skLineSegment(sketch, "E386", {"start": v(-5.72, -4.86) * mm, "end": v(-5.72, -5) * mm});
            skLineSegment(sketch, "E387", {"start": v(-5.72, -5) * mm, "end": v(-5.71, -5.16) * mm});
            skLineSegment(sketch, "E388", {"start": v(-5.71, -5.16) * mm, "end": v(-5.7, -5.3) * mm});
            skLineSegment(sketch, "E389", {"start": v(-5.7, -5.3) * mm, "end": v(-5.54, -5.3) * mm});
            skLineSegment(sketch, "E390", {"start": v(-5.54, -5.3) * mm, "end": v(-5.4, -5.29) * mm});
            skLineSegment(sketch, "E391", {"start": v(-5.4, -5.29) * mm, "end": v(-5.24, -5.26) * mm});
            skLineSegment(sketch, "E392", {"start": v(-5.24, -5.26) * mm, "end": v(-5.1, -5.23) * mm});
            skLineSegment(sketch, "E393", {"start": v(-5.1, -5.23) * mm, "end": v(-4.95, -5.18) * mm});
            skLineSegment(sketch, "E394", {"start": v(-4.95, -5.18) * mm, "end": v(-4.82, -5.13) * mm});
            skLineSegment(sketch, "E395", {"start": v(-4.82, -5.13) * mm, "end": v(-4.68, -5.06) * mm});
            skLineSegment(sketch, "E396", {"start": v(-4.68, -5.06) * mm, "end": v(-4.55, -5) * mm});
            skLineSegment(sketch, "E397", {"start": v(-4.55, -5) * mm, "end": v(-4.42, -4.91) * mm});
            skLineSegment(sketch, "E398", {"start": v(-4.42, -4.91) * mm, "end": v(-4.3, -4.83) * mm});
            skLineSegment(sketch, "E399", {"start": v(-4.3, -4.83) * mm, "end": v(-4.18, -4.73) * mm});
            skLineSegment(sketch, "E400", {"start": v(-4.18, -4.73) * mm, "end": v(-4.08, -4.63) * mm});
            skLineSegment(sketch, "E401", {"start": v(-4.08, -4.63) * mm, "end": v(-4, -4.5) * mm});
            skLineSegment(sketch, "E402", {"start": v(-4, -4.5) * mm, "end": v(-3.9, -4.36) * mm});
            skLineSegment(sketch, "E403", {"start": v(-3.9, -4.36) * mm, "end": v(-3.82, -4.23) * mm});
            skLineSegment(sketch, "E404", {"start": v(-3.82, -4.23) * mm, "end": v(-3.74, -4.1) * mm});
            skLineSegment(sketch, "E405", {"start": v(-3.74, -4.1) * mm, "end": v(-3.65, -3.97) * mm});
            skLineSegment(sketch, "E406", {"start": v(-3.65, -3.97) * mm, "end": v(-3.57, -3.83) * mm});
            skLineSegment(sketch, "E407", {"start": v(-3.57, -3.83) * mm, "end": v(-3.48, -3.7) * mm});
            skLineSegment(sketch, "E408", {"start": v(-3.48, -3.7) * mm, "end": v(-3.4, -3.57) * mm});
            skLineSegment(sketch, "E409", {"start": v(-3.4, -3.57) * mm, "end": v(-3.31, -3.44) * mm});
            skLineSegment(sketch, "E410", {"start": v(-3.31, -3.44) * mm, "end": v(-3.23, -3.3) * mm});
            skLineSegment(sketch, "E411", {"start": v(-3.23, -3.3) * mm, "end": v(-3.08, -3.37) * mm});
            skLineSegment(sketch, "E412", {"start": v(-3.08, -3.37) * mm, "end": v(-2.94, -3.44) * mm});
            skLineSegment(sketch, "E413", {"start": v(-2.94, -3.44) * mm, "end": v(-2.8, -3.5) * mm});
            skLineSegment(sketch, "E414", {"start": v(-2.8, -3.5) * mm, "end": v(-2.65, -3.57) * mm});
            skLineSegment(sketch, "E415", {"start": v(-2.65, -3.57) * mm, "end": v(-2.51, -3.63) * mm});
            skLineSegment(sketch, "E416", {"start": v(-2.51, -3.63) * mm, "end": v(-2.37, -3.7) * mm});
            skLineSegment(sketch, "E417", {"start": v(-2.37, -3.7) * mm, "end": v(-2.23, -3.76) * mm});
            skLineSegment(sketch, "E418", {"start": v(-2.23, -3.76) * mm, "end": v(-2.21, -3.77) * mm});
            skLineSegment(sketch, "E419", {"start": v(-2.21, -3.77) * mm, "end": v(-2.25, -3.92) * mm});
            skLineSegment(sketch, "E420", {"start": v(-2.25, -3.92) * mm, "end": v(-2.3, -4.07) * mm});
            skLineSegment(sketch, "E421", {"start": v(-2.3, -4.07) * mm, "end": v(-2.34, -4.22) * mm});
            skLineSegment(sketch, "E422", {"start": v(-2.34, -4.22) * mm, "end": v(-2.39, -4.37) * mm});
            skLineSegment(sketch, "E423", {"start": v(-2.39, -4.37) * mm, "end": v(-2.43, -4.52) * mm});
            skLineSegment(sketch, "E424", {"start": v(-2.43, -4.52) * mm, "end": v(-2.48, -4.67) * mm});
            skLineSegment(sketch, "E425", {"start": v(-2.48, -4.67) * mm, "end": v(-2.52, -4.83) * mm});
            skLineSegment(sketch, "E426", {"start": v(-2.52, -4.83) * mm, "end": v(-2.56, -4.98) * mm});
            skLineSegment(sketch, "E427", {"start": v(-2.56, -4.98) * mm, "end": v(-2.6, -5.13) * mm});
            skLineSegment(sketch, "E428", {"start": v(-2.6, -5.13) * mm, "end": v(-2.65, -5.28) * mm});
            skLineSegment(sketch, "E429", {"start": v(-2.65, -5.28) * mm, "end": v(-2.66, -5.43) * mm});
            skLineSegment(sketch, "E430", {"start": v(-2.66, -5.43) * mm, "end": v(-2.66, -5.58) * mm});
            skLineSegment(sketch, "E431", {"start": v(-2.66, -5.58) * mm, "end": v(-2.64, -5.73) * mm});
            skLineSegment(sketch, "E432", {"start": v(-2.64, -5.73) * mm, "end": v(-2.62, -5.88) * mm});
            skLineSegment(sketch, "E433", {"start": v(-2.62, -5.88) * mm, "end": v(-2.59, -6.03) * mm});
            skLineSegment(sketch, "E434", {"start": v(-2.59, -6.03) * mm, "end": v(-2.55, -6.17) * mm});
            skLineSegment(sketch, "E435", {"start": v(-2.55, -6.17) * mm, "end": v(-2.5, -6.32) * mm});
            skLineSegment(sketch, "E436", {"start": v(-2.5, -6.32) * mm, "end": v(-2.43, -6.45) * mm});
            skLineSegment(sketch, "E437", {"start": v(-2.43, -6.45) * mm, "end": v(-2.36, -6.59) * mm});
            skLineSegment(sketch, "E438", {"start": v(-2.36, -6.59) * mm, "end": v(-2.29, -6.7) * mm});
            skLineSegment(sketch, "E439", {"start": v(-2.29, -6.7) * mm, "end": v(-2.2, -6.83) * mm});
            skLineSegment(sketch, "E440", {"start": v(-2.2, -6.83) * mm, "end": v(-2.1, -6.95) * mm});
            skLineSegment(sketch, "E441", {"start": v(-2.1, -6.95) * mm, "end": v(-1.97, -6.86) * mm});
            skLineSegment(sketch, "E442", {"start": v(-1.97, -6.86) * mm, "end": v(-1.86, -6.77) * mm});
            skLineSegment(sketch, "E443", {"start": v(-1.86, -6.77) * mm, "end": v(-1.74, -6.66) * mm});
            skLineSegment(sketch, "E444", {"start": v(-1.74, -6.66) * mm, "end": v(-1.64, -6.56) * mm});
            skLineSegment(sketch, "E445", {"start": v(-1.64, -6.56) * mm, "end": v(-1.54, -6.44) * mm});
            skLineSegment(sketch, "E446", {"start": v(-1.54, -6.44) * mm, "end": v(-1.45, -6.33) * mm});
            skLineSegment(sketch, "E447", {"start": v(-1.45, -6.33) * mm, "end": v(-1.37, -6.2) * mm});
            skLineSegment(sketch, "E448", {"start": v(-1.37, -6.2) * mm, "end": v(-1.3, -6.07) * mm});
            skLineSegment(sketch, "E449", {"start": v(-1.3, -6.07) * mm, "end": v(-1.24, -5.92) * mm});
            skLineSegment(sketch, "E450", {"start": v(-1.24, -5.92) * mm, "end": v(-1.18, -5.8) * mm});
            skLineSegment(sketch, "E451", {"start": v(-1.18, -5.8) * mm, "end": v(-1.14, -5.64) * mm});
            skLineSegment(sketch, "E452", {"start": v(-1.14, -5.64) * mm, "end": v(-1.1, -5.5) * mm});
            skLineSegment(sketch, "E453", {"start": v(-1.1, -5.5) * mm, "end": v(-1.1, -5.34) * mm});
            skLineSegment(sketch, "E454", {"start": v(-1.1, -5.34) * mm, "end": v(-1.1, -5.19) * mm});
            skLineSegment(sketch, "E455", {"start": v(-1.1, -5.19) * mm, "end": v(-1.1, -5.03) * mm});
            skLineSegment(sketch, "E456", {"start": v(-1.1, -5.03) * mm, "end": v(-1.1, -4.87) * mm});
            skLineSegment(sketch, "E457", {"start": v(-1.1, -4.87) * mm, "end": v(-1.1, -4.71) * mm});
            skLineSegment(sketch, "E458", {"start": v(-1.1, -4.71) * mm, "end": v(-1.1, -4.56) * mm});
            skLineSegment(sketch, "E459", {"start": v(-1.1, -4.56) * mm, "end": v(-1.1, -4.4) * mm});
            skLineSegment(sketch, "E460", {"start": v(-1.1, -4.4) * mm, "end": v(-1.1, -4.24) * mm});
            skLineSegment(sketch, "E461", {"start": v(-1.1, -4.24) * mm, "end": v(-1.1, -4.09) * mm});
            skLineSegment(sketch, "E462", {"start": v(-1.1, -4.09) * mm, "end": v(-1.1, -3.93) * mm});
            skLineSegment(sketch, "E463", {"start": v(-1.1, -3.93) * mm, "end": v(-0.95, -3.9) * mm});
            skLineSegment(sketch, "E464", {"start": v(-0.95, -3.9) * mm, "end": v(-0.8, -3.88) * mm});
            skLineSegment(sketch, "E465", {"start": v(-0.8, -3.88) * mm, "end": v(-0.64, -3.86) * mm});
            skLineSegment(sketch, "E466", {"start": v(-0.64, -3.86) * mm, "end": v(-0.48, -3.84) * mm});
            skLineSegment(sketch, "E467", {"start": v(-0.48, -3.84) * mm, "end": v(-0.32, -3.82) * mm});
            skLineSegment(sketch, "E468", {"start": v(-0.32, -3.82) * mm, "end": v(-0.17, -3.8) * mm});
            skLineSegment(sketch, "E469", {"start": v(-0.17, -3.8) * mm, "end": v(-0.01, -3.77) * mm});
            skLineSegment(sketch, "E470", {"start": v(-0.01, -3.77) * mm, "end": v(0, -3.77) * mm});
            skLineSegment(sketch, "E471", {"start": v(0, -3.77) * mm, "end": v(0.05, -3.92) * mm});
            skLineSegment(sketch, "E472", {"start": v(0.05, -3.92) * mm, "end": v(0.1, -4.07) * mm});
            skLineSegment(sketch, "E473", {"start": v(0.1, -4.07) * mm, "end": v(0.14, -4.22) * mm});
            skLineSegment(sketch, "E474", {"start": v(0.14, -4.22) * mm, "end": v(0.18, -4.37) * mm});
            skLineSegment(sketch, "E475", {"start": v(0.18, -4.37) * mm, "end": v(0.22, -4.52) * mm});
            skLineSegment(sketch, "E476", {"start": v(0.22, -4.52) * mm, "end": v(0.27, -4.67) * mm});
            skLineSegment(sketch, "E477", {"start": v(0.27, -4.67) * mm, "end": v(0.31, -4.83) * mm});
            skLineSegment(sketch, "E478", {"start": v(0.31, -4.83) * mm, "end": v(0.36, -4.98) * mm});
            skLineSegment(sketch, "E479", {"start": v(0.36, -4.98) * mm, "end": v(0.4, -5.13) * mm});
            skLineSegment(sketch, "E480", {"start": v(0.4, -5.13) * mm, "end": v(0.45, -5.28) * mm});
            skLineSegment(sketch, "E481", {"start": v(0.45, -5.28) * mm, "end": v(0.53, -5.41) * mm});
            skLineSegment(sketch, "E482", {"start": v(0.53, -5.41) * mm, "end": v(0.6, -5.53) * mm});
            skLineSegment(sketch, "E483", {"start": v(0.6, -5.53) * mm, "end": v(0.7, -5.66) * mm});
            skLineSegment(sketch, "E484", {"start": v(0.7, -5.66) * mm, "end": v(0.8, -5.77) * mm});
            skLineSegment(sketch, "E485", {"start": v(0.8, -5.77) * mm, "end": v(0.9, -5.88) * mm});
            skLineSegment(sketch, "E486", {"start": v(0.9, -5.88) * mm, "end": v(1.02, -5.97) * mm});
            skLineSegment(sketch, "E487", {"start": v(1.02, -5.97) * mm, "end": v(1.14, -6.06) * mm});
            skLineSegment(sketch, "E488", {"start": v(1.14, -6.06) * mm, "end": v(1.26, -6.14) * mm});
            skLineSegment(sketch, "E489", {"start": v(1.26, -6.14) * mm, "end": v(1.4, -6.22) * mm});
            skLineSegment(sketch, "E490", {"start": v(1.4, -6.22) * mm, "end": v(1.53, -6.28) * mm});
            skLineSegment(sketch, "E491", {"start": v(1.53, -6.28) * mm, "end": v(1.68, -6.34) * mm});
            skLineSegment(sketch, "E492", {"start": v(1.68, -6.34) * mm, "end": v(1.81, -6.38) * mm});
            skLineSegment(sketch, "E493", {"start": v(1.81, -6.38) * mm, "end": v(1.87, -6.24) * mm});
            skLineSegment(sketch, "E494", {"start": v(1.87, -6.24) * mm, "end": v(1.92, -6.1) * mm});
            skLineSegment(sketch, "E495", {"start": v(1.92, -6.1) * mm, "end": v(1.96, -5.95) * mm});
            skLineSegment(sketch, "E496", {"start": v(1.96, -5.95) * mm, "end": v(2, -5.81) * mm});
            skLineSegment(sketch, "E497", {"start": v(2, -5.81) * mm, "end": v(2.01, -5.65) * mm});
            skLineSegment(sketch, "E498", {"start": v(2.01, -5.65) * mm, "end": v(2.02, -5.51) * mm});
            skLineSegment(sketch, "E499", {"start": v(2.02, -5.51) * mm, "end": v(2.02, -5.35) * mm});
            skLineSegment(sketch, "E500", {"start": v(2.02, -5.35) * mm, "end": v(2.01, -5.21) * mm});
            skLineSegment(sketch, "E501", {"start": v(2.01, -5.21) * mm, "end": v(1.99, -5.05) * mm});
            skLineSegment(sketch, "E502", {"start": v(1.99, -5.05) * mm, "end": v(1.96, -4.91) * mm});
            skLineSegment(sketch, "E503", {"start": v(1.96, -4.91) * mm, "end": v(1.92, -4.76) * mm});
            skLineSegment(sketch, "E504", {"start": v(1.92, -4.76) * mm, "end": v(1.87, -4.63) * mm});
            skLineSegment(sketch, "E505", {"start": v(1.87, -4.63) * mm, "end": v(1.79, -4.5) * mm});
            skLineSegment(sketch, "E506", {"start": v(1.79, -4.5) * mm, "end": v(1.7, -4.36) * mm});
            skLineSegment(sketch, "E507", {"start": v(1.7, -4.36) * mm, "end": v(1.62, -4.23) * mm});
            skLineSegment(sketch, "E508", {"start": v(1.62, -4.23) * mm, "end": v(1.53, -4.1) * mm});
            skLineSegment(sketch, "E509", {"start": v(1.53, -4.1) * mm, "end": v(1.45, -3.97) * mm});
            skLineSegment(sketch, "E510", {"start": v(1.45, -3.97) * mm, "end": v(1.36, -3.83) * mm});
            skLineSegment(sketch, "E511", {"start": v(1.36, -3.83) * mm, "end": v(1.28, -3.7) * mm});
            skLineSegment(sketch, "E512", {"start": v(1.28, -3.7) * mm, "end": v(1.2, -3.57) * mm});
            skLineSegment(sketch, "E513", {"start": v(1.2, -3.57) * mm, "end": v(1.1, -3.44) * mm});
            skLineSegment(sketch, "E514", {"start": v(1.1, -3.44) * mm, "end": v(1.02, -3.3) * mm});
            skLineSegment(sketch, "E515", {"start": v(1.02, -3.3) * mm, "end": v(1.14, -3.2) * mm});
            skLineSegment(sketch, "E516", {"start": v(1.14, -3.2) * mm, "end": v(1.26, -3.1) * mm});
            skLineSegment(sketch, "E517", {"start": v(1.26, -3.1) * mm, "end": v(1.38, -3) * mm});
            skLineSegment(sketch, "E518", {"start": v(1.38, -3) * mm, "end": v(1.5, -2.9) * mm});
            skLineSegment(sketch, "E519", {"start": v(1.5, -2.9) * mm, "end": v(1.62, -2.79) * mm});
            skLineSegment(sketch, "E520", {"start": v(1.62, -2.79) * mm, "end": v(1.73, -2.69) * mm});
            skLineSegment(sketch, "E521", {"start": v(1.73, -2.69) * mm, "end": v(1.85, -2.58) * mm});
            skLineSegment(sketch, "E522", {"start": v(1.85, -2.58) * mm, "end": v(1.87, -2.57) * mm});
            skLineSegment(sketch, "E523", {"start": v(1.87, -2.57) * mm, "end": v(1.98, -2.68) * mm});
            skLineSegment(sketch, "E524", {"start": v(1.98, -2.68) * mm, "end": v(2.1, -2.78) * mm});
            skLineSegment(sketch, "E525", {"start": v(2.1, -2.78) * mm, "end": v(2.22, -2.88) * mm});
            skLineSegment(sketch, "E526", {"start": v(2.22, -2.88) * mm, "end": v(2.34, -2.98) * mm});
            skLineSegment(sketch, "E527", {"start": v(2.34, -2.98) * mm, "end": v(2.46, -3.09) * mm});
            skLineSegment(sketch, "E528", {"start": v(2.46, -3.09) * mm, "end": v(2.58, -3.2) * mm});
            skLineSegment(sketch, "E529", {"start": v(2.58, -3.2) * mm, "end": v(2.7, -3.3) * mm});
            skLineSegment(sketch, "E530", {"start": v(2.7, -3.3) * mm, "end": v(2.82, -3.4) * mm});
            skLineSegment(sketch, "E531", {"start": v(2.82, -3.4) * mm, "end": v(2.93, -3.5) * mm});
            skLineSegment(sketch, "E532", {"start": v(2.93, -3.5) * mm, "end": v(3.05, -3.6) * mm});
            skLineSegment(sketch, "E533", {"start": v(3.05, -3.6) * mm, "end": v(3.2, -3.67) * mm});
            skLineSegment(sketch, "E534", {"start": v(3.2, -3.67) * mm, "end": v(3.32, -3.73) * mm});
            skLineSegment(sketch, "E535", {"start": v(3.32, -3.73) * mm, "end": v(3.47, -3.78) * mm});
            skLineSegment(sketch, "E536", {"start": v(3.47, -3.78) * mm, "end": v(3.61, -3.82) * mm});
            skLineSegment(sketch, "E537", {"start": v(3.61, -3.82) * mm, "end": v(3.77, -3.86) * mm});
            skLineSegment(sketch, "E538", {"start": v(3.77, -3.86) * mm, "end": v(3.9, -3.88) * mm});
            skLineSegment(sketch, "E539", {"start": v(3.9, -3.88) * mm, "end": v(4.06, -3.89) * mm});
            skLineSegment(sketch, "E540", {"start": v(4.06, -3.89) * mm, "end": v(4.2, -3.89) * mm});
            skLineSegment(sketch, "E541", {"start": v(4.2, -3.89) * mm, "end": v(4.36, -3.88) * mm});
            skLineSegment(sketch, "E542", {"start": v(4.36, -3.88) * mm, "end": v(4.5, -3.86) * mm});
            skLineSegment(sketch, "E543", {"start": v(4.5, -3.86) * mm, "end": v(4.66, -3.83) * mm});
            skLineSegment(sketch, "E544", {"start": v(4.66, -3.83) * mm, "end": v(4.8, -3.8) * mm});
            skLineSegment(sketch, "E545", {"start": v(4.8, -3.8) * mm, "end": v(4.77, -3.64) * mm});
            skLineSegment(sketch, "E546", {"start": v(4.77, -3.64) * mm, "end": v(4.74, -3.5) * mm});
            skLineSegment(sketch, "E547", {"start": v(4.74, -3.5) * mm, "end": v(4.7, -3.35) * mm});
            skLineSegment(sketch, "E548", {"start": v(4.7, -3.35) * mm, "end": v(4.64, -3.22) * mm});
            skLineSegment(sketch, "E549", {"start": v(4.64, -3.22) * mm, "end": v(4.57, -3.07) * mm});
            skLineSegment(sketch, "E550", {"start": v(4.57, -3.07) * mm, "end": v(4.5, -2.95) * mm});
            skLineSegment(sketch, "E551", {"start": v(4.5, -2.95) * mm, "end": v(4.42, -2.82) * mm});
            skLineSegment(sketch, "E552", {"start": v(4.42, -2.82) * mm, "end": v(4.33, -2.7) * mm});
            skLineSegment(sketch, "E553", {"start": v(4.33, -2.7) * mm, "end": v(4.23, -2.58) * mm});
            skLineSegment(sketch, "E554", {"start": v(4.23, -2.58) * mm, "end": v(4.13, -2.48) * mm});
            skLineSegment(sketch, "E555", {"start": v(4.13, -2.48) * mm, "end": v(4.01, -2.37) * mm});
            skLineSegment(sketch, "E556", {"start": v(4.01, -2.37) * mm, "end": v(3.9, -2.28) * mm});
            skLineSegment(sketch, "E557", {"start": v(3.9, -2.28) * mm, "end": v(3.76, -2.22) * mm});
            skLineSegment(sketch, "E558", {"start": v(3.76, -2.22) * mm, "end": v(3.61, -2.15) * mm});
            skLineSegment(sketch, "E559", {"start": v(3.61, -2.15) * mm, "end": v(3.47, -2.09) * mm});
            skLineSegment(sketch, "E560", {"start": v(3.47, -2.09) * mm, "end": v(3.33, -2.02) * mm});
            skLineSegment(sketch, "E561", {"start": v(3.33, -2.02) * mm, "end": v(3.19, -1.96) * mm});
            skLineSegment(sketch, "E562", {"start": v(3.19, -1.96) * mm, "end": v(3.04, -1.9) * mm});
            skLineSegment(sketch, "E563", {"start": v(3.04, -1.9) * mm, "end": v(2.9, -1.83) * mm});
            skLineSegment(sketch, "E564", {"start": v(2.9, -1.83) * mm, "end": v(2.76, -1.76) * mm});
            skLineSegment(sketch, "E565", {"start": v(2.76, -1.76) * mm, "end": v(2.61, -1.7) * mm});
            skLineSegment(sketch, "E566", {"start": v(2.61, -1.7) * mm, "end": v(2.47, -1.63) * mm});
            skLineSegment(sketch, "E567", {"start": v(2.47, -1.63) * mm, "end": v(2.52, -1.48) * mm});
            skLineSegment(sketch, "E568", {"start": v(2.52, -1.48) * mm, "end": v(2.56, -1.33) * mm});
            skLineSegment(sketch, "E569", {"start": v(2.56, -1.33) * mm, "end": v(2.6, -1.18) * mm});
            skLineSegment(sketch, "E570", {"start": v(2.6, -1.18) * mm, "end": v(2.65, -1.03) * mm});
            skLineSegment(sketch, "E571", {"start": v(2.65, -1.03) * mm, "end": v(2.7, -0.88) * mm});
            skLineSegment(sketch, "E572", {"start": v(2.7, -0.88) * mm, "end": v(2.74, -0.73) * mm});
            skLineSegment(sketch, "E573", {"start": v(2.74, -0.73) * mm, "end": v(2.78, -0.57) * mm});
            skLineSegment(sketch, "E574", {"start": v(2.78, -0.57) * mm, "end": v(2.79, -0.56) * mm});
            skCircle(sketch, "E575", {"center": v(-1.1, 0) * mm, "radius": 1.5 * mm});
            skLineSegment(sketch, "E576", {"start": v(-1.1, 1.5) * mm, "end": v(-1.1, -1) * mm, "construction": true});
            skLineSegment(sketch, "E577", {"start": v(-2.22, -1) * mm, "end": v(0.01, -1) * mm});
            skSolve(sketch);
        }
        {
            var Q0;
            {var subQ0=sQuery(id+"F0.wireOp",EDGE,"E577");Q0=makeQuery(id+"F0.imprint","IMPRINT",FACE,{"disambiguationData":[TD([[makeQuery(id+"F0.imprint","IMPRINT",EDGE,{"derivedFrom":subQ0}),-1.0]])]});}
            var Q1;
            Q1=makeQuery(id+"F0.imprint","IMPRINT",FACE,{"disambiguationData":[TD([[makeQuery(id+"F0.imprint","IMPRINT",EDGE,{"derivedFrom":sQuery(id+"F0.wireOp",EDGE,"E0")}),1.0]])]});
            extrude(context, id + "F1", {"entities" : qUnion([Q0, Q1]), "depth" : 7 * mm});
        }
    });
